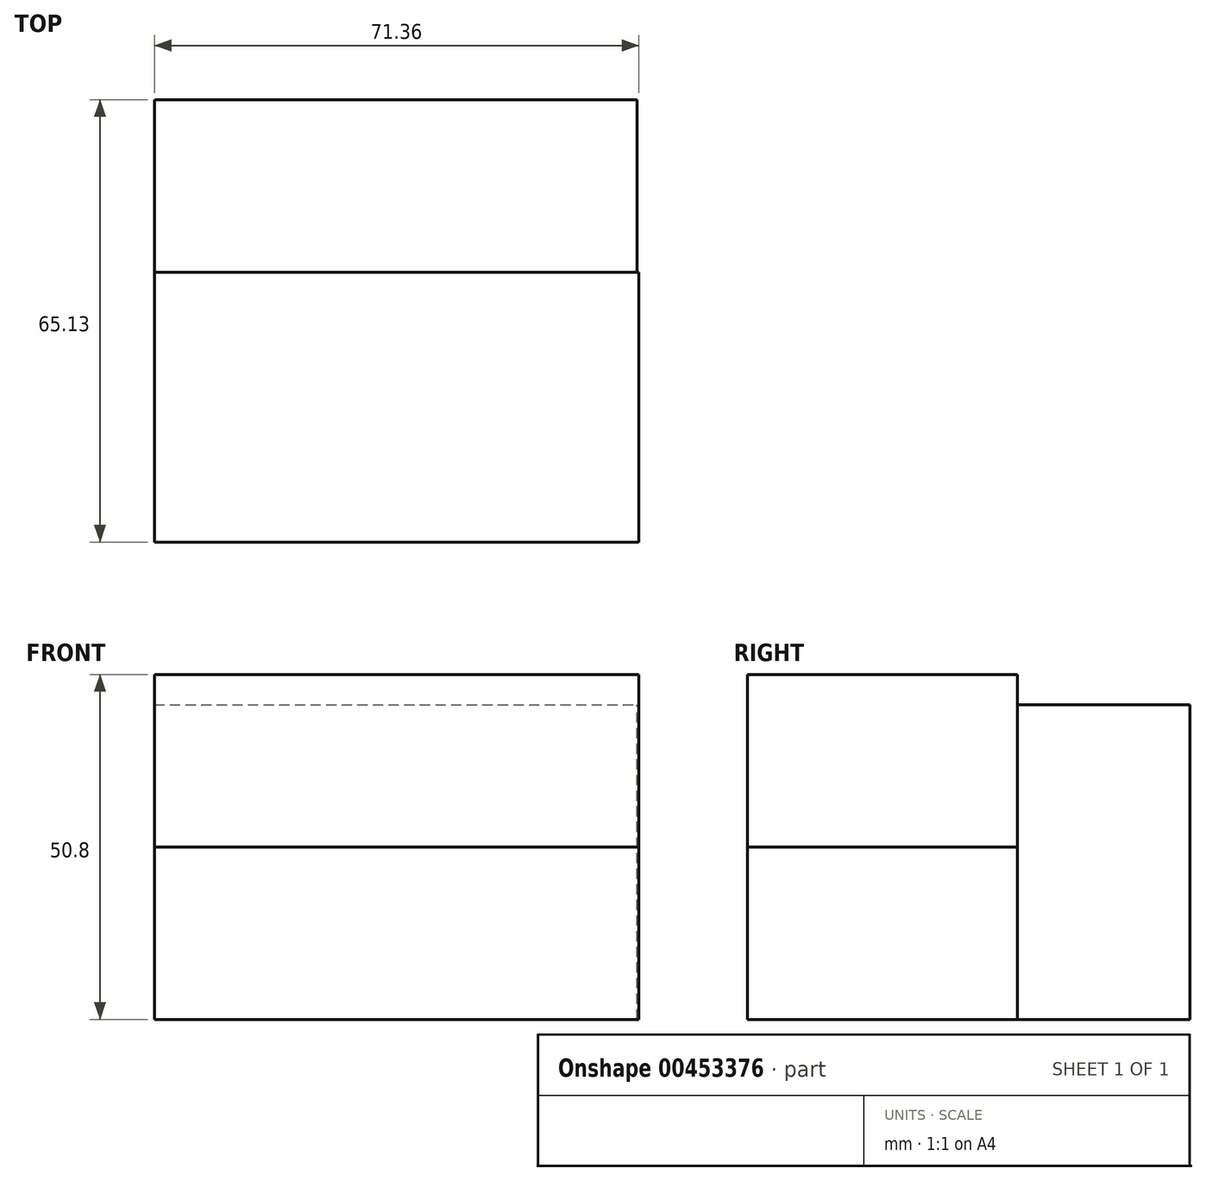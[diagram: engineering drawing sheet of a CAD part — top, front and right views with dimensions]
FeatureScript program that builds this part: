
annotation { "Feature Type Name" : "Feature", "Feature Type Description" : "" }
export const myFeature = defineFeature(function(context is Context, id is Id, definition is map)
    precondition{}
    {
        {
            var Q0;
            Q0=qCreatedBy(makeId("Front.planeOp"),FACE);
            var sketch = newSketch(context, id + "F0", { "sketchPlane" : qUnion([Q0])});
            skLineSegment(sketch, "E0.bottom", {"start": v(-42.2, 0) * mm, "end": v(28.85, 0) * mm});
            skLineSegment(sketch, "E0.top", {"start": v(-42.2, 46.3) * mm, "end": v(28.85, 46.3) * mm});
            skLineSegment(sketch, "E0.left", {"start": v(-42.2, 0) * mm, "end": v(-42.2, 46.3) * mm});
            skLineSegment(sketch, "E0.right", {"start": v(28.85, 0) * mm, "end": v(28.85, 46.3) * mm});
            skSolve(sketch);
        }
        {
            var Q0;
            Q0 = qSketchRegion(id + "F0", true);
            extrude(context, id + "F1", {"entities" : qUnion([Q0]), "depth" : 25.4 * mm});
        }
        {
            var Q0;
            Q0=makeQuery(id+"F1.opExtrude","SWEPT_FACE",FACE,{"disambiguationData":[OSD([sQuery(id+"F0.wireOp",EDGE,"E0.bottom")])]});
            var sketch = newSketch(context, id + "F2", { "sketchPlane" : qUnion([Q0])});
            skLineSegment(sketch, "E1.bottom", {"start": v(-42.2, 25.4) * mm, "end": v(29.15, 25.4) * mm});
            skLineSegment(sketch, "E1.top", {"start": v(-42.2, 65.13) * mm, "end": v(29.15, 65.13) * mm});
            skLineSegment(sketch, "E1.left", {"start": v(-42.2, 25.4) * mm, "end": v(-42.2, 65.13) * mm});
            skLineSegment(sketch, "E1.right", {"start": v(29.15, 25.4) * mm, "end": v(29.15, 65.13) * mm});
            skSolve(sketch);
        }
        {
            var Q0;
            Q0 = qSketchRegion(id + "F2", true);
            extrude(context, id + "F3", {"entities" : qUnion([Q0]), "oppositeDirection" : true, "depth" : 25.4 * mm});
        }
        {
            var Q0;
            Q0=makeQuery(id+"F3.opExtrude","CAP_FACE",FACE,{"disambiguationData":[OSD([sQuery(id+"F2.wireOp",EDGE,"E1.bottom"),sQuery(id+"F2.wireOp",EDGE,"E1.top"),sQuery(id+"F2.wireOp",EDGE,"E1.left"),sQuery(id+"F2.wireOp",EDGE,"E1.right")])],"isStart":false});
            extrude(context, id + "F4", {"entities" : qUnion([Q0]), "depth" : 25.4 * mm});
        }
    });
